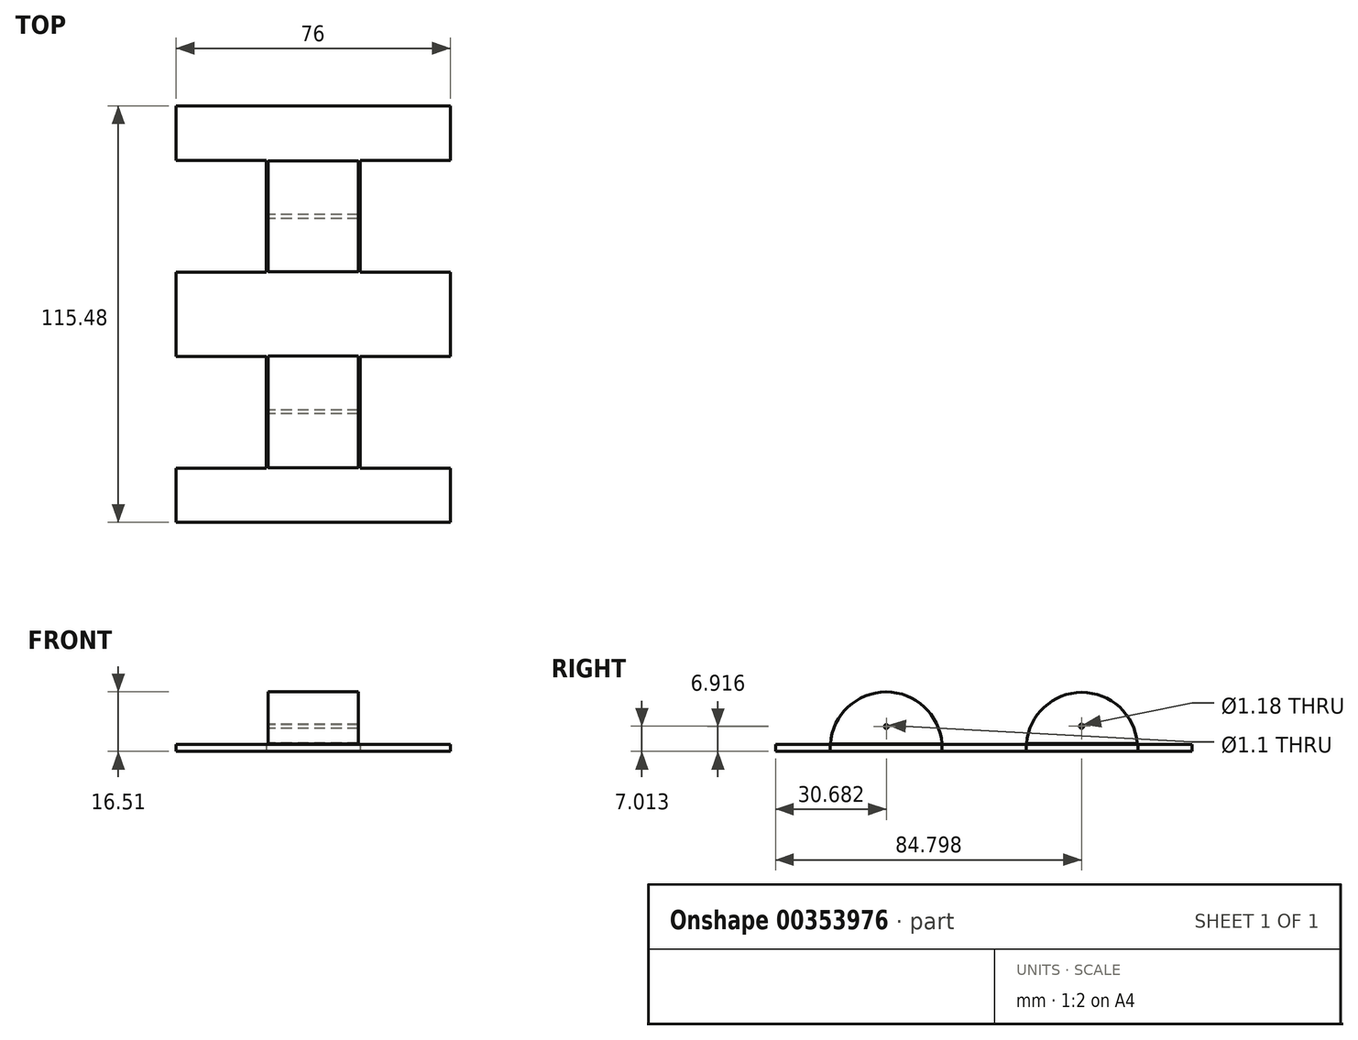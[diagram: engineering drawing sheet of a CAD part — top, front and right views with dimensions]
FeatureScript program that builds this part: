
annotation { "Feature Type Name" : "Feature", "Feature Type Description" : "" }
export const myFeature = defineFeature(function(context is Context, id is Id, definition is map)
    precondition{}
    {
        {
            var Q0;
            Q0=qCreatedBy(makeId("Top.planeOp"),FACE);
            var sketch = newSketch(context, id + "F0", { "sketchPlane" : qUnion([Q0])});
            skLineSegment(sketch, "E0.bottom", {"start": v(38, -57.74) * mm, "end": v(-38, -57.74) * mm});
            skLineSegment(sketch, "E0.top", {"start": v(38, 57.74) * mm, "end": v(-38, 57.74) * mm});
            skLineSegment(sketch, "E0.left", {"start": v(38, -57.74) * mm, "end": v(38, -42.67) * mm});
            skLineSegment(sketch, "E0.right", {"start": v(-38, -57.74) * mm, "end": v(-38, -42.67) * mm});
            skPoint(sketch, "E0.middle", {"position": v(0, 0) * mm});
            skLineSegment(sketch, "E1.bottom", {"start": v(-38, 42.67) * mm, "end": v(-13, 42.67) * mm});
            skLineSegment(sketch, "E1.top", {"start": v(-38, 11.67) * mm, "end": v(-13, 11.67) * mm});
            skLineSegment(sketch, "E1.right", {"start": v(-13, 42.67) * mm, "end": v(-13, 11.67) * mm});
            skLineSegment(sketch, "E2.MirrorCS", {"start": v(13, 42.67) * mm, "end": v(13, 11.67) * mm});
            skLineSegment(sketch, "E3.MirrorCS", {"start": v(38, 11.67) * mm, "end": v(13, 11.67) * mm});
            skLineSegment(sketch, "E4.MirrorCS", {"start": v(38, 42.67) * mm, "end": v(13, 42.67) * mm});
            skLineSegment(sketch, "E5.MirrorCS", {"start": v(-38, -11.67) * mm, "end": v(-13, -11.67) * mm});
            skLineSegment(sketch, "E6.MirrorCS", {"start": v(-13, -42.67) * mm, "end": v(-13, -11.67) * mm});
            skLineSegment(sketch, "E7.MirrorCS", {"start": v(-38, -42.67) * mm, "end": v(-13, -42.67) * mm});
            skLineSegment(sketch, "E8.MirrorCS", {"start": v(38, -11.67) * mm, "end": v(13, -11.67) * mm});
            skLineSegment(sketch, "E9.MirrorCS", {"start": v(13, -42.67) * mm, "end": v(13, -11.67) * mm});
            skLineSegment(sketch, "E10.MirrorCS", {"start": v(38, -42.67) * mm, "end": v(13, -42.67) * mm});
            skLineSegment(sketch, "E11.trimOffspring", {"start": v(38, 42.67) * mm, "end": v(38, 57.74) * mm});
            skLineSegment(sketch, "E12.trimOffspring", {"start": v(38, -11.67) * mm, "end": v(38, 11.67) * mm});
            skLineSegment(sketch, "E13.trimOffspring", {"start": v(-38, -11.67) * mm, "end": v(-38, 11.67) * mm});
            skLineSegment(sketch, "E14.trimOffspring", {"start": v(-38, 42.67) * mm, "end": v(-38, 57.74) * mm});
            skSolve(sketch);
        }
        {
            var Q0;
            Q0 = qSketchRegion(id + "F0", true);
            extrude(context, id + "F1", {"entities" : qUnion([Q0]), "endBound" : BoundingType.SYMMETRIC, "depth" : 2 * mm});
        }
        {
            var Q0;
            Q0=qCreatedBy(makeId("Right.planeOp"),FACE);
            var sketch = newSketch(context, id + "F2", { "sketchPlane" : qUnion([Q0])});
            skArc(sketch, "E15", {"start": v(42.5, 1.3) * mm, "mid": v(27.1, 15.4) * mm, "end": v(11.8, 1.2) * mm});
            skArc(sketch, "E16", {"start": v(-11.64, 1.2) * mm, "mid": v(-27.16, 15.51) * mm, "end": v(-42.58, 1.1) * mm});
            skCircle(sketch, "E17", {"center": v(27.06, 6.01) * mm, "radius": 0.59 * mm});
            skCircle(sketch, "E18", {"center": v(-27.06, 5.92) * mm, "radius": 0.55 * mm});
            skLineSegment(sketch, "E19", {"start": v(42.5, 1.3) * mm, "end": v(11.8, 1.2) * mm});
            skLineSegment(sketch, "E20", {"start": v(-11.64, 1.2) * mm, "end": v(-42.58, 1.1) * mm});
            skSolve(sketch);
        }
        {
            var Q0;
            Q0 = qSketchRegion(id + "F2", true);
            extrude(context, id + "F3", {"entities" : qUnion([Q0]), "endBound" : BoundingType.SYMMETRIC, "depth" : 25 * mm});
        }
    });
